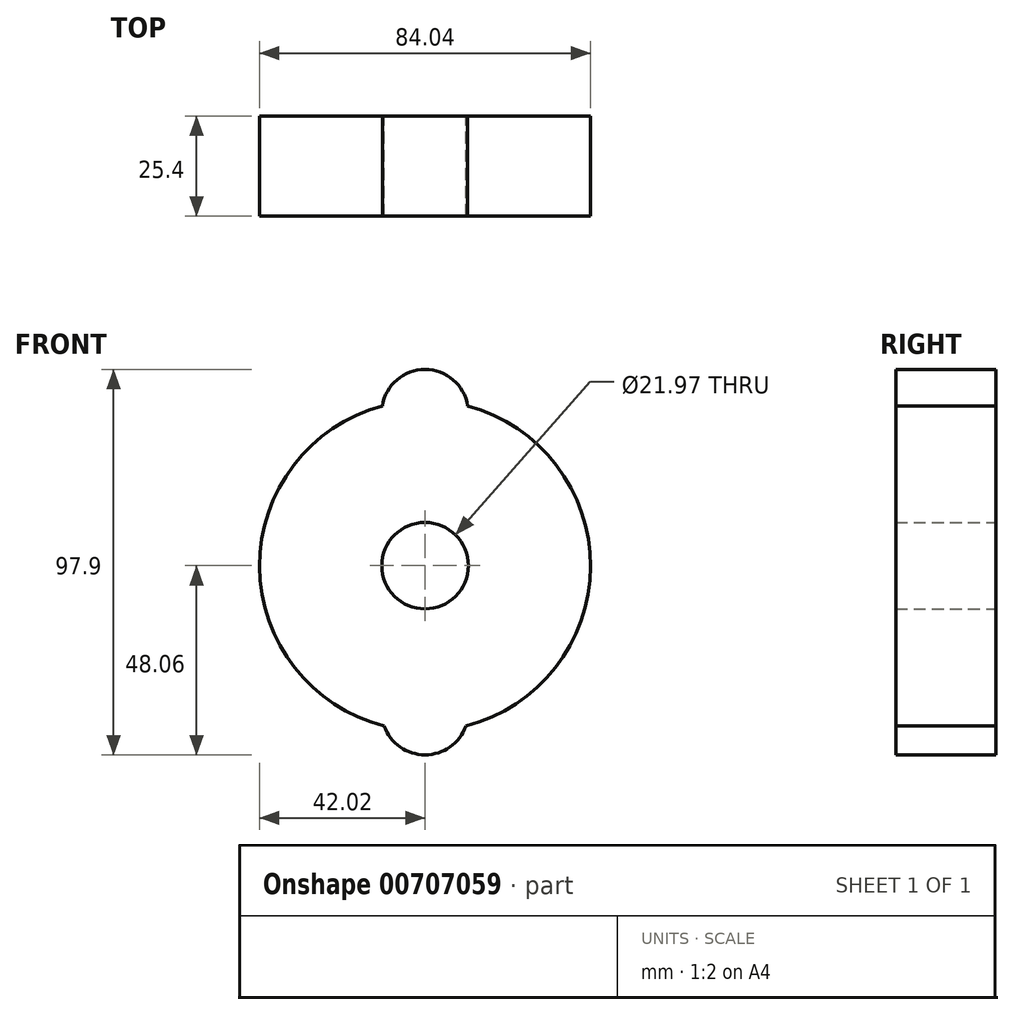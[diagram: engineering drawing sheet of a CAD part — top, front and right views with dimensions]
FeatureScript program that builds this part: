
annotation { "Feature Type Name" : "Feature", "Feature Type Description" : "" }
export const myFeature = defineFeature(function(context is Context, id is Id, definition is map)
    precondition{}
    {
        {
            var Q0;
            Q0=qCreatedBy(makeId("Front.planeOp"),FACE);
            var sketch = newSketch(context, id + "F0", { "sketchPlane" : qUnion([Q0])});
            skCircle(sketch, "E0", {"center": v(0, 0) * mm, "radius": 42.02 * mm});
            skCircle(sketch, "E1", {"center": v(0, 0) * mm, "radius": 10.99 * mm});
            skCircle(sketch, "E2", {"center": v(0, -37.07) * mm, "radius": 10.99 * mm});
            skCircle(sketch, "E3", {"center": v(0, 38.86) * mm, "radius": 10.99 * mm});
            skSolve(sketch);
        }
        {
            var Q0;
            Q0 = qSketchRegion(id + "F0", true);
            extrude(context, id + "F1", {"entities" : qUnion([Q0]), "depth" : 25.4 * mm, "offsetDistance" : 25.4 * mm});
        }
    });
